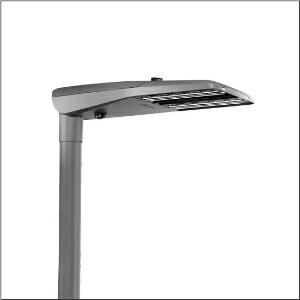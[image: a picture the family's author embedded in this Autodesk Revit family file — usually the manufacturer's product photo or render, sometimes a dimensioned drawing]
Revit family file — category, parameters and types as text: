
# Revit family: streetlight_sl_11_iq_midi___st1_2a_5xc3a51y08me_2b41
name_source: partatom
category: Lighting Fixtures
units: mm (PartAtom-declared; Revit-internal decimal feet)

## family parameters
Cut with Voids When Loaded = No
Host = Face
Light Source = No
Part Type = Normal
Room Calculation Point = No
Round Connector Dimension = Use Diameter
Shared = No

## types (1)
- --- (1 x LED, 18110 lm, 122.7 W, 3000K)
    Apparent Load = 123 VA
    CIE Flux Codes = 32 70 96 100 100
    Color Rendering = 70
    Color Temperature = 3000K
    Default Elevation = 1800 mm
    Description = Streetlight SL 11 iQ midi, mast luminaire, primary light control with 3 zone facetted reflector, of plastic, silver coated, highly specular, primary optical cover: cover, of PMMA, transparent, light distribution: ST1.2a, light emission: direct distribution, primary light characteristic: asymmetric, installation type: post-top, side-entry, LED, High Power LED, rated luminous flux: 18.110lm, luminous efficacy: 148lm/W, light colour: 730, colour temperature: 3000K, control: presetting dimming logarithmic, Street-Remote, Auto-Match, Temp-Guard, Lumen-Switch, Night-Set, Smart-Wire, Light-Fading, Desk-Remote (wireless, voltage-free reading and setting of iQ features in the workshop via application-optimized NFC function/RFID function), optimised constant luminous flux control (CLO 2.0), with cable H07RN-F 5x 1.5mm², mains connection: 230..240V, AC, 50/60Hz, connection cable pre-assembled, cable length: 12,5m, start of lifetime: 123W, end of service life: 130W, reduction: 56W, luminaire housing, of diecast aluminium, powder-coated, Siteco® metallic grey (DB 702S), please order mast flange separately, inclination adjustable without tools: 0°, 5°, 10°, 15° (post-top) | 0°, -5°, -10°, -15° (side-entry), sealing non-destructively replaceable, multi-level sealing system, length: 780mm, width: 376mm, height: 118mm, mast flange for spigot size: 42mm (side-entry): 5XC10008XM4, 60/48mm (side-entry/post-top): 5XC10108XM2, 76/60mm (side-entry/post-top): 5XC10108XM1, equipment: Power, Smart Interface below and above, protection rating (complete): IP66, insulation class (complete): insulation class II (safety insulation), certification: CE, ENEC, VDE, UKCA, impact resistance: IK09, permissible operating ambient temperature for outdoor applications: -25..+50°C, standard-compliant lighting for roads and squares, Environmental Product Declaration (EPD) tested and certified by an independent institute, packaging unit: 1 piece

Light Distribution: ST1.2a
    Height = 118 mm
    Lamp = 1 x LED
    Lamp Light Flux = 18110 lm
    Lamp Power = 122.7 W
    Lamp count = 1
    Length = 780 mm
    Luminous efficacy = 148 lm/W
    Manufacturer = Siteco
    ModVariant = No
    Model = 5XC3A51Y08ME
    Number of Poles = 1
    OnlyDefault = Yes
    Power Factor = 1
    Product Name = Streetlight SL 11 iQ midi | ST1.2a
    Product group = mast luminaire | pylon top
    ProductGroupID = 6100
    Protection Class = Protection class II
    Protection Degree = IP 66
    RLX_Detail_Level = 1
    RLX_Emergency_Light_Flux = 0 lm
    RLX_Emergency_Type = 0
    RLX_Emergency_Type_DB = No
    RlxData = <blob elided: 69749 chars, md5=b0a7308e>
    Socket = socket
    Standby Power = 0 W
    System Light Flux = 18111 lm
    System Power = 123 W
    Type Comments = factory setting: luminous flux: 100 % | dim-lin: 254 | 553 mA
    Type Image = l_1004429.jpg
    URL = http://relux.com
    VarID = @adj_082643
    Voltage = 0 V
    Weight = 0.00 kg
    Width = 376 mm

## geometry (parser evidence)
native form markers: Blend x4, Sweep x11
no freeform markers — native parametric forms only
